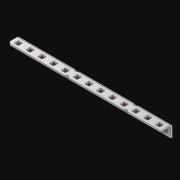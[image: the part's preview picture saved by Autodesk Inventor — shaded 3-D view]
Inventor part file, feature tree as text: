
AUTODESK INVENTOR PART (.ipt)
format: ipt  version: 2021 (Build 250183000, 183)  size: 648,704 bytes
history: native  units: in
note: dims shown in document units (in); Inventor stores cm internally (conversion verified against a paired STEP export)
features: extrude x27, other x26, sketch x3, pattern_linear x1, sheet_metal_op x1
ambient origin geometry x8: Origin, YZ Plane, XZ Plane, XY Plane, X Axis, Y Axis, Z Axis, Center Point
bodies: Solid1 (feature_tree)
feature tree (58):
  pattern_linear  "Rectangular Pattern1"  Spacing1=0.063in  [1 undecoded]
  extrude  "Extrusion1"  Depth=0.5in
  sketch  "Sketch1"  dims[d0=0.182in]
  other  "Srf1"
  sketch  "Sketch2"  dims[d1=0.063in d2=0.0in]
  other  "Srf2"
  other  "Srf3"
  other  "Srf5"
  other  "Srf7"
  other  "Srf9"
  other  "Srf11"
  other  "Srf13"
  other  "Srf15"
  other  "Srf17"
  other  "Srf19"
  other  "Srf21"
  other  "Srf23"
  other  "Srf25"
  other  "Srf4"
  other  "Srf6"
  other  "Srf8"
  other  "Srf10"
  other  "Srf12"
  other  "Srf14"
  other  "Srf16"
  other  "Srf18"
  other  "Srf20"
  other  "Srf22"
  other  "Srf24"
  other  "Srf26"
  sketch  "Sketch3"  dims[d3=0.182in d4=0.063in d5=0.0in d8=0.5in d9=11.0in d10=0.0in]
  sheet_metal_op  "Fold1"
  extrude  "ExtrusionSrf1"  Depth=0.5in TaperAngle=0.0deg
  extrude  "ExtrusionSrf2"  [1 undecoded]
  extrude  "ExtrusionSrf3"  [1 undecoded]
  extrude  "ExtrusionSrf4"  [1 undecoded]
  extrude  "ExtrusionSrf5"  [1 undecoded]
  extrude  "ExtrusionSrf6"  [1 undecoded]
  extrude  "ExtrusionSrf7"  [1 undecoded]
  extrude  "ExtrusionSrf8"  [1 undecoded]
  extrude  "ExtrusionSrf9"  [1 undecoded]
  extrude  "ExtrusionSrf10"  [1 undecoded]
  extrude  "ExtrusionSrf11"  [1 undecoded]
  extrude  "ExtrusionSrf12"  [1 undecoded]
  extrude  "ExtrusionSrf13"  [1 undecoded]
  extrude  "ExtrusionSrf14"  [1 undecoded]
  extrude  "ExtrusionSrf37"  [1 undecoded]
  extrude  "ExtrusionSrf38"  [1 undecoded]
  extrude  "ExtrusionSrf39"  [1 undecoded]
  extrude  "ExtrusionSrf40"  [1 undecoded]
  extrude  "ExtrusionSrf41"  [1 undecoded]
  extrude  "ExtrusionSrf42"  [1 undecoded]
  extrude  "ExtrusionSrf43"  [1 undecoded]
  extrude  "ExtrusionSrf44"  [1 undecoded]
  extrude  "ExtrusionSrf45"  [1 undecoded]
  extrude  "ExtrusionSrf46"  [1 undecoded]
  extrude  "ExtrusionSrf47"  [1 undecoded]
  extrude  "ExtrusionSrf48"  [1 undecoded]
note: 26 required parameter values undecoded (feature->parameter linkage not recoverable at this tier; creation-order binding heuristic only, values carry confidence <= 0.55)
